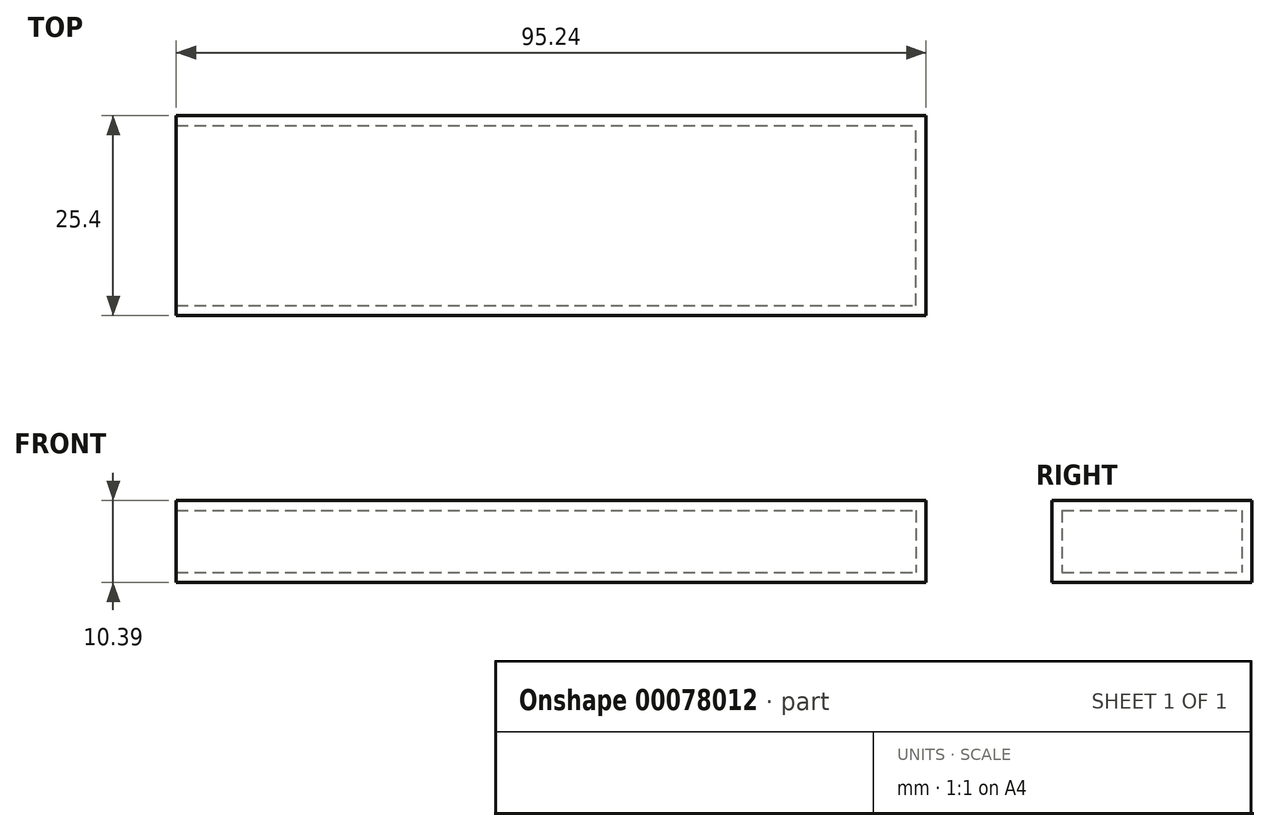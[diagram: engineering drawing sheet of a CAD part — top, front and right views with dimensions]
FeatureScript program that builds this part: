
annotation { "Feature Type Name" : "Feature", "Feature Type Description" : "" }
export const myFeature = defineFeature(function(context is Context, id is Id, definition is map)
    precondition{}
    {
        {
            var Q0;
            Q0=qCreatedBy(makeId("Front.planeOp"),FACE);
            var sketch = newSketch(context, id + "F0", { "sketchPlane" : qUnion([Q0])});
            skLineSegment(sketch, "E0.bottom", {"start": v(-19.34, 12.57) * mm, "end": v(75.9, 12.57) * mm});
            skLineSegment(sketch, "E0.top", {"start": v(-19.34, 2.18) * mm, "end": v(75.9, 2.18) * mm});
            skLineSegment(sketch, "E0.left", {"start": v(-19.34, 12.57) * mm, "end": v(-19.34, 2.18) * mm});
            skLineSegment(sketch, "E0.right", {"start": v(75.9, 12.57) * mm, "end": v(75.9, 2.18) * mm});
            skSolve(sketch);
        }
        {
            var Q0;
            Q0=makeQuery(id+"F0.imprint","IMPRINT",FACE,{"disambiguationData":[TD([[makeQuery(id+"F0.imprint","IMPRINT",EDGE,{"derivedFrom":sQuery(id+"F0.wireOp",EDGE,"E0.bottom")}),-1.0]])]});
            extrude(context, id + "F1", {"entities" : qUnion([Q0]), "depth" : 25.4 * mm});
        }
        {
            var Q0;
            Q0=makeQuery(id+"F1.opExtrude","SWEPT_FACE",FACE,{"disambiguationData":[OSD([sQuery(id+"F0.wireOp",EDGE,"E0.left")])]});
            shell(context, id + "F2", {"entities" : qUnion([Q0]), "thickness" : 1.27 * mm});
        }
    });
